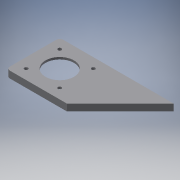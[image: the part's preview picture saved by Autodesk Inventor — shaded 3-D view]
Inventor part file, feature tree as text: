
AUTODESK INVENTOR PART (.ipt)
format: ipt  version: 2018 (Build 220112000, 112)  size: 164,352 bytes
history: native  units: mm
features: other x6, extrude x3, sketch x3, fillet x2
ambient origin geometry x8: Origin, YZ Plane, XZ Plane, XY Plane, X Axis, Y Axis, Z Axis, Center Point
bodies: Body1 (feature_tree)
feature tree (14):
  other  "Sólido1"
  extrude  "Extrusão1"  Depth=120.0mm
  extrude  "Extrusão6"  Depth=9.52mm TaperAngle=0.0deg
  extrude  "Extrusão7"  Depth=59.0mm
  fillet  "Arredondamento1"  Radius=5.0mm
  fillet  "Arredondamento2"  Radius=5.0mm
  sketch  "Esboço1"  dims[d0=120.0mm d1=120.0mm]
  other  "Referência1"
  other  "Referência2"
  sketch  "Esboço9"  dims[d2=80.0mm d3=9.52mm d4=0.0mm]
  sketch  "Esboço10"  dims[d72=59.0mm d73=59.0mm d74=5.0mm d75=5.0mm d76=5.0mm d77=5.0mm d78=23.57mm d79=23.57mm d80=23.57mm d81=23.57mm d82=23.57mm d83=23.57mm d84=23.57mm d85=23.57mm d86=8.0mm d87=8.0mm d88=40.0mm d89=6.52mm d90=0.0mm d91=6.52mm d92=0.0mm d93=6.0mm d94=5.0mm]
  other  "<userpath>\Documents\OpenCNC\MONTAGEM\CNC1.iam"
  other  "CNC1.iam"
  other  "PERFIL_ESTRUTURAL_40X80_EIXO_Y:1"
